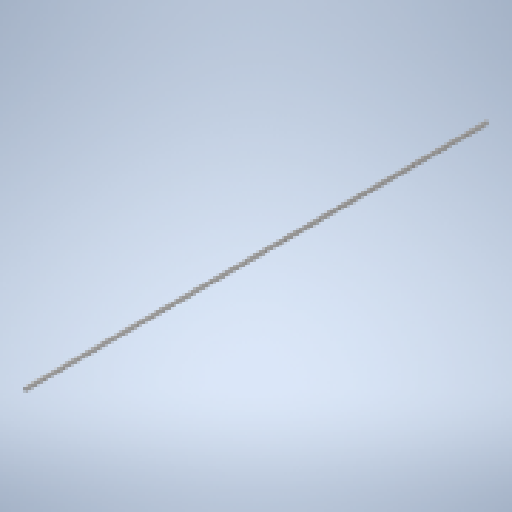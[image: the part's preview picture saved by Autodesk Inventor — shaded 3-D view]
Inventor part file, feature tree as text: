
AUTODESK INVENTOR PART (.ipt)
format: ipt  version: 2025.1 (Build 291241000, 241)  size: 136,192 bytes
history: native  units: mm
features: other x1, extrude x1
ambient origin geometry x8: Origin, YZ Plane, XZ Plane, XY Plane, X Axis, Y Axis, Z Axis, Center Point
bodies: Body1 (feature_tree)
feature tree (2):
  other  "Sólido1"
  extrude  "Extrusão1"  Depth=8.0mm
